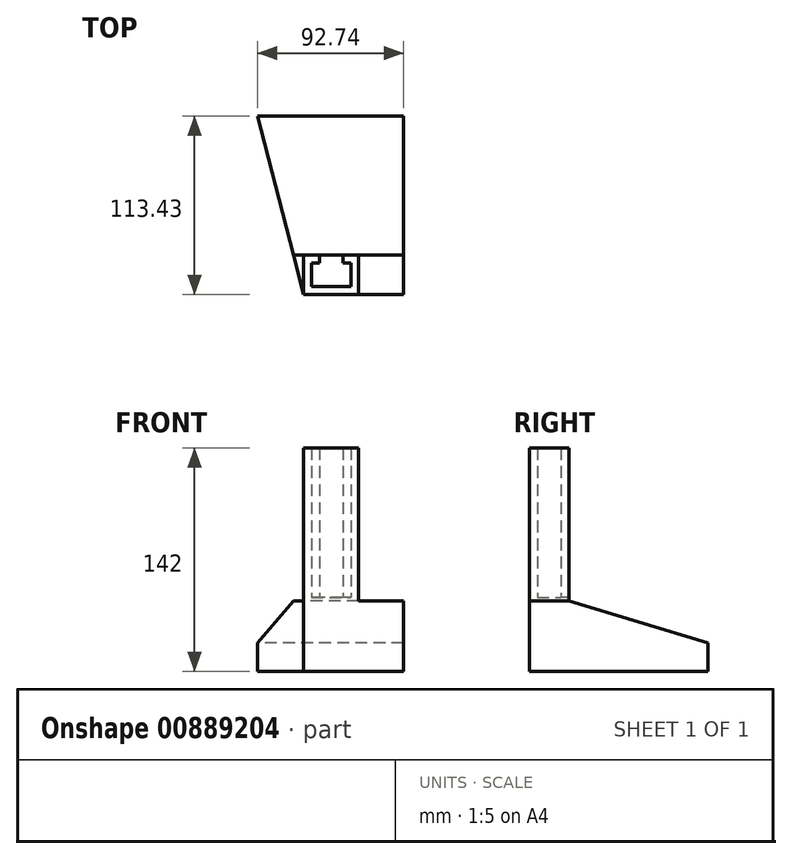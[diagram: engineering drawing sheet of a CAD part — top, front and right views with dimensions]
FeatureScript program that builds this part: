
annotation { "Feature Type Name" : "Feature", "Feature Type Description" : "" }
export const myFeature = defineFeature(function(context is Context, id is Id, definition is map)
    precondition{}
    {
        {
            var Q0;
            Q0=qCreatedBy(makeId("Top.planeOp"),FACE);
            var sketch = newSketch(context, id + "F0", { "sketchPlane" : qUnion([Q0])});
            skLineSegment(sketch, "E0.bottom", {"start": v(13.19, -11.22) * mm, "end": v(-21.81, -11.22) * mm});
            skLineSegment(sketch, "E0.left", {"start": v(13.19, -11.22) * mm, "end": v(13.19, 13.78) * mm});
            skLineSegment(sketch, "E0.right", {"start": v(-21.81, -11.22) * mm, "end": v(-21.81, 13.78) * mm});
            skLineSegment(sketch, "E1", {"start": v(13.19, 13.78) * mm, "end": v(3.19, 13.78) * mm});
            skLineSegment(sketch, "E2", {"start": v(3.19, 13.78) * mm, "end": v(3.19, 8.78) * mm});
            skLineSegment(sketch, "E3", {"start": v(-11.81, 8.78) * mm, "end": v(-11.81, 13.78) * mm});
            skLineSegment(sketch, "E4", {"start": v(-11.81, 13.78) * mm, "end": v(-21.81, 13.78) * mm});
            skLineSegment(sketch, "E5", {"start": v(-11.81, 8.78) * mm, "end": v(-16.81, 8.78) * mm});
            skLineSegment(sketch, "E6", {"start": v(-16.81, 8.78) * mm, "end": v(-16.81, -6.22) * mm});
            skLineSegment(sketch, "E7", {"start": v(-16.81, -6.22) * mm, "end": v(8.19, -6.22) * mm});
            skLineSegment(sketch, "E8", {"start": v(8.19, -6.22) * mm, "end": v(8.19, 8.78) * mm});
            skLineSegment(sketch, "E9", {"start": v(8.19, 8.78) * mm, "end": v(3.19, 8.78) * mm});
            skSolve(sketch);
        }
        {
            var Q0;
            Q0 = qSketchRegion(id + "F0", true);
            extrude(context, id + "F1", {"entities" : qUnion([Q0]), "depth" : 95 * mm, "offsetDistance" : 25 * mm});
        }
        {
            var Q0;
            Q0=makeQuery(id+"F1.opExtrude","CAP_FACE",FACE,{"disambiguationData":[OSD([sQuery(id+"F0.wireOp",EDGE,"E0.bottom"),sQuery(id+"F0.wireOp",EDGE,"E0.left"),sQuery(id+"F0.wireOp",EDGE,"E0.right"),sQuery(id+"F0.wireOp",EDGE,"E1"),sQuery(id+"F0.wireOp",EDGE,"E2"),sQuery(id+"F0.wireOp",EDGE,"E3"),sQuery(id+"F0.wireOp",EDGE,"E4"),sQuery(id+"F0.wireOp",EDGE,"E5"),sQuery(id+"F0.wireOp",EDGE,"E6"),sQuery(id+"F0.wireOp",EDGE,"E7"),sQuery(id+"F0.wireOp",EDGE,"E8"),sQuery(id+"F0.wireOp",EDGE,"E9")])],"isStart":true});
            var sketch = newSketch(context, id + "F2", { "sketchPlane" : qUnion([Q0])});
            skLineSegment(sketch, "E10.bottom", {"start": v(13.19, -13.78) * mm, "end": v(-21.81, -13.78) * mm});
            skLineSegment(sketch, "E10.top", {"start": v(13.19, 11.22) * mm, "end": v(-21.81, 11.22) * mm});
            skLineSegment(sketch, "E10.left", {"start": v(13.19, -13.78) * mm, "end": v(13.19, 11.22) * mm});
            skLineSegment(sketch, "E10.right", {"start": v(-21.81, -13.78) * mm, "end": v(-21.81, 11.22) * mm});
            skSolve(sketch);
        }
        {
            var Q0;
            Q0 = qSketchRegion(id + "F2", true);
            extrude(context, id + "F3", {"entities" : qUnion([Q0]), "operationType" : NewBodyOperationType.ADD, "depth" : 2 * mm, "offsetDistance" : 25 * mm});
        }
        {
            var Q0;
            Q0=makeQuery(id+"F3.opExtrude","CAP_FACE",FACE,{"disambiguationData":[OSD([sQuery(id+"F2.wireOp",EDGE,"E10.bottom"),sQuery(id+"F2.wireOp",EDGE,"E10.top"),sQuery(id+"F2.wireOp",EDGE,"E10.left"),sQuery(id+"F2.wireOp",EDGE,"E10.right")])],"isStart":false});
            var sketch = newSketch(context, id + "F4", { "sketchPlane" : qUnion([Q0])});
            skLineSegment(sketch, "E11.bottom", {"start": v(-51.12, 11.22) * mm, "end": v(41.62, 11.22) * mm});
            skLineSegment(sketch, "E11.top", {"start": v(-51.12, -102.21) * mm, "end": v(41.62, -102.21) * mm});
            skLineSegment(sketch, "E11.left", {"start": v(-51.12, 11.22) * mm, "end": v(-51.12, -102.21) * mm});
            skLineSegment(sketch, "E11.right", {"start": v(41.62, 11.22) * mm, "end": v(41.62, -102.21) * mm});
            skSolve(sketch);
        }
        {
            var Q0;
            Q0 = qSketchRegion(id + "F4", true);
            extrude(context, id + "F5", {"entities" : qUnion([Q0]), "operationType" : NewBodyOperationType.ADD, "depth" : 45 * mm, "offsetDistance" : 25 * mm});
        }
        {
            var Q0;
            Q0=makeQuery(id+"F5.opExtrude","SWEPT_FACE",FACE,{"disambiguationData":[OSD([sQuery(id+"F4.wireOp",EDGE,"E11.left")])]});
            var sketch = newSketch(context, id + "F6", { "sketchPlane" : qUnion([Q0])});
            skLineSegment(sketch, "E12", {"start": v(-13.78, -2) * mm, "end": v(-102.21, -28.78) * mm});
            skLineSegment(sketch, "E13", {"start": v(-102.21, -28.78) * mm, "end": v(-102.21, -2) * mm});
            skLineSegment(sketch, "E14", {"start": v(-102.21, -2) * mm, "end": v(-13.78, -2) * mm});
            skSolve(sketch);
        }
        {
            var Q0;
            Q0 = qSketchRegion(id + "F6", true);
            extrude(context, id + "F7", {"entities" : qUnion([Q0]), "operationType" : NewBodyOperationType.REMOVE, "endBound" : BoundingType.UP_TO_NEXT, "oppositeDirection" : true, "depth" : 25 * mm, "offsetDistance" : 25 * mm});
        }
        {
            var Q0;
            Q0=makeQuery(id+"F3.opExtrude","CAP_VERTEX",VERTEX,{"disambiguationData":[OSD([sQuery(id+"F2.wireOp",EDGE,"E10.top"),sQuery(id+"F2.wireOp",EDGE,"E10.right")])],"isStart":false});
            var Q1;
            Q1=makeQuery(id+"F7.boolean.opBoolean","COPY",VERTEX,{"derivedFrom":makeQuery(id+"F7.opExtrude","CAP_VERTEX",VERTEX,{"disambiguationData":[OSD([sQuery(id+"F4.wireOp",EDGE,"E11.top"),sQuery(id+"F4.wireOp",EDGE,"E11.left"),sQuery(id+"F6.wireOp",EDGE,"E12"),sQuery(id+"F6.wireOp",EDGE,"E13")])],"isStart":true})});
            var Q2;
            Q2=makeQuery(id+"F5.opExtrude","CAP_VERTEX",VERTEX,{"disambiguationData":[OSD([sQuery(id+"F4.wireOp",EDGE,"E11.top"),sQuery(id+"F4.wireOp",EDGE,"E11.left")])],"isStart":false});
            cPlane(context, id + "F8", {"entities" : qUnion([Q0, Q1, Q2]), "cplaneType" : CPlaneType.THREE_POINT, "offset" : 25 * mm, "width" : 150 * mm, "height" : 150 * mm});
        }
        {
            var Q0;
            Q0=qCreatedBy(id+"F8.planeOp",FACE);
            var sketch = newSketch(context, id + "F9", { "sketchPlane" : qUnion([Q0])});
            skLineSegment(sketch, "E15", {"start": v(-5.4, -2) * mm, "end": v(111.75, 32.37) * mm});
            skLineSegment(sketch, "E16", {"start": v(111.75, 32.37) * mm, "end": v(111.75, -47) * mm});
            skLineSegment(sketch, "E17", {"start": v(111.75, -47) * mm, "end": v(-6.06, -47) * mm});
            skLineSegment(sketch, "E18", {"start": v(-6.06, -47) * mm, "end": v(-5.4, -2) * mm});
            skSolve(sketch);
        }
        {
            var Q0;
            Q0 = qSketchRegion(id + "F9", true);
            extrude(context, id + "F10", {"entities" : qUnion([Q0]), "operationType" : NewBodyOperationType.REMOVE, "oppositeDirection" : true, "depth" : 47.8 * mm, "offsetDistance" : 25 * mm});
        }
    });
